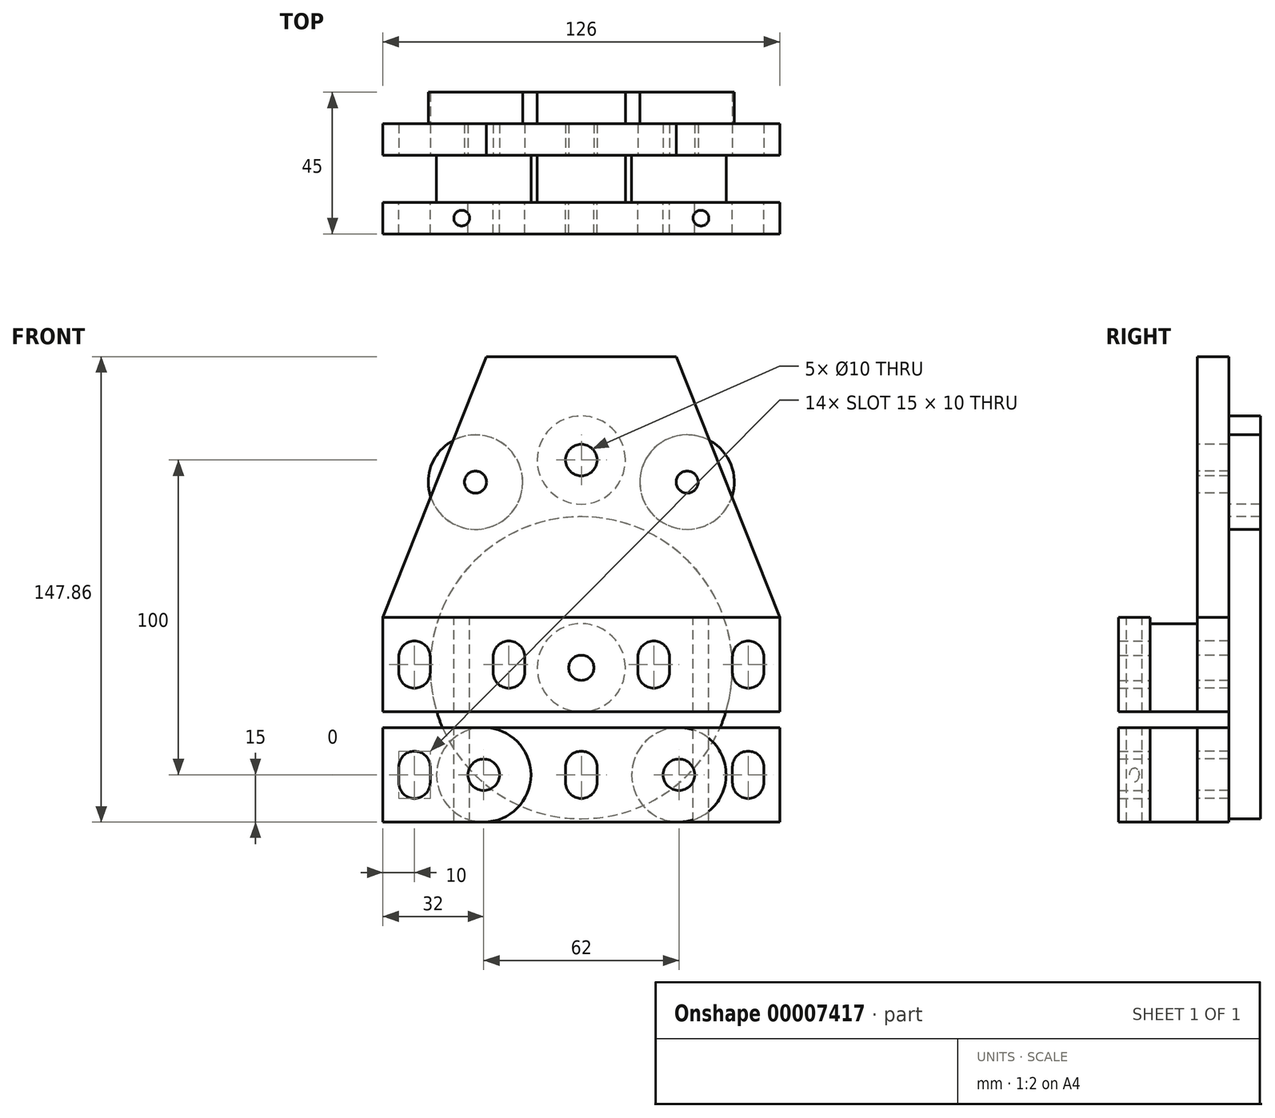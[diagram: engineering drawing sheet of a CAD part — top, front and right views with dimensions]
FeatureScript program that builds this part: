
annotation { "Feature Type Name" : "Feature", "Feature Type Description" : "" }
export const myFeature = defineFeature(function(context is Context, id is Id, definition is map)
    precondition{}
    {
        {
            var Q0;
            Q0=qCreatedBy(makeId("Front.planeOp"),FACE);
            var sketch = newSketch(context, id + "F0", { "sketchPlane" : qUnion([Q0])});
            skCircle(sketch, "E0", {"center": v(0, 0) * mm, "radius": 14 * mm});
            skCircle(sketch, "E1", {"center": v(0, 0) * mm, "radius": 48 * mm});
            skLineSegment(sketch, "E2", {"start": v(-81.34, -49) * mm, "end": v(130.56, -49) * mm, "construction": true});
            skCircle(sketch, "E3", {"center": v(-31, -34) * mm, "radius": 15 * mm});
            skLineSegment(sketch, "E4", {"start": v(0, 0) * mm, "end": v(0, -49) * mm, "construction": true});
            skLineSegment(sketch, "E5", {"start": v(-81.34, -52.2) * mm, "end": v(130.56, -52.2) * mm, "construction": true});
            skLineSegment(sketch, "E6", {"start": v(130.56, -51.2) * mm, "end": v(-81.34, -51.2) * mm, "construction": true});
            skCircle(sketch, "E7.MirrorC", {"center": v(31, -34) * mm, "radius": 15 * mm});
            skCircle(sketch, "E8", {"center": v(-63, -34) * mm, "radius": 15 * mm, "construction": true});
            skCircle(sketch, "E9.MirrorC", {"center": v(63, -34) * mm, "radius": 15 * mm, "construction": true});
            skLineSegment(sketch, "E10", {"start": v(71.6, 114.85) * mm, "end": v(71.6, 34.85) * mm});
            skLineSegment(sketch, "E11", {"start": v(71.6, 34.85) * mm, "end": v(91.6, 34.85) * mm});
            skLineSegment(sketch, "E12", {"start": v(91.6, 34.85) * mm, "end": v(91.6, 64.85) * mm});
            skLineSegment(sketch, "E13", {"start": v(91.6, 64.85) * mm, "end": v(141.6, 64.85) * mm});
            skLineSegment(sketch, "E14", {"start": v(141.6, 64.85) * mm, "end": v(141.6, 34.85) * mm});
            skLineSegment(sketch, "E15", {"start": v(141.6, 34.85) * mm, "end": v(161.6, 34.85) * mm});
            skLineSegment(sketch, "E16", {"start": v(161.6, 34.85) * mm, "end": v(161.6, 114.85) * mm});
            skLineSegment(sketch, "E17", {"start": v(161.6, 114.85) * mm, "end": v(71.6, 114.85) * mm});
            skLineSegment(sketch, "E18", {"start": v(-14, 0) * mm, "end": v(-14, -49) * mm, "construction": true});
            skLineSegment(sketch, "E19", {"start": v(-16, -34) * mm, "end": v(-14, -34) * mm, "construction": true});
            skLineSegment(sketch, "E20", {"start": v(-31, -19) * mm, "end": v(0, -19) * mm, "construction": true});
            skPoint(sketch, "E21", {"position": v(0, -14) * mm});
            skSolve(sketch);
        }
        {
            var Q0;
            Q0=qCreatedBy(makeId("Front.planeOp"),FACE);
            var sketch = newSketch(context, id + "F1", { "sketchPlane" : qUnion([Q0])});
            skCircle(sketch, "E22.0", {"center": v(0, 0) * mm, "radius": 14 * mm, "construction": true});
            skLineSegment(sketch, "E23", {"start": v(-63, 16) * mm, "end": v(-63, -14) * mm});
            skLineSegment(sketch, "E24", {"start": v(-63, -14) * mm, "end": v(63, -14) * mm});
            skLineSegment(sketch, "E25", {"start": v(63, -14) * mm, "end": v(63, 16) * mm});
            skLineSegment(sketch, "E26", {"start": v(63, 16) * mm, "end": v(-63, 16) * mm});
            skCircle(sketch, "E27", {"center": v(0, 0) * mm, "radius": 4 * mm});
            skLineSegment(sketch, "E28.bottom", {"start": v(-63, -19) * mm, "end": v(63, -19) * mm});
            skLineSegment(sketch, "E28.top", {"start": v(-63, -49) * mm, "end": v(63, -49) * mm});
            skLineSegment(sketch, "E28.left", {"start": v(-63, -19) * mm, "end": v(-63, -49) * mm});
            skLineSegment(sketch, "E28.right", {"start": v(63, -19) * mm, "end": v(63, -49) * mm});
            skLineSegment(sketch, "E29", {"start": v(0, 0) * mm, "end": v(0, -19) * mm, "construction": true});
            skLineSegment(sketch, "E30", {"start": v(-48, -34) * mm, "end": v(-46, -34) * mm, "construction": true});
            skLineSegment(sketch, "E31", {"start": v(-46, -34) * mm, "end": v(-31, -34) * mm, "construction": true});
            skLineSegment(sketch, "E32", {"start": v(-53, -36.5) * mm, "end": v(-53, -31.5) * mm, "construction": true});
            skArc(sketch, "E33.0.startCap", {"start": v(-48, -36.5) * mm, "mid": v(-53, -41.5) * mm, "end": v(-58, -36.5) * mm});
            skArc(sketch, "E33.0.endCap", {"start": v(-58, -31.5) * mm, "mid": v(-53, -26.5) * mm, "end": v(-48, -31.5) * mm});
            skLineSegment(sketch, "E33.0.left", {"start": v(-58, -36.5) * mm, "end": v(-58, -31.5) * mm});
            skLineSegment(sketch, "E33.0.right", {"start": v(-48, -36.5) * mm, "end": v(-48, -31.5) * mm});
            skLineSegment(sketch, "E34", {"start": v(-58, -34) * mm, "end": v(-63, -34) * mm, "construction": true});
            skLineSegment(sketch, "E35", {"start": v(0, -31.5) * mm, "end": v(0, -36.5) * mm, "construction": true});
            skArc(sketch, "E36.0.startCap", {"start": v(-5, -31.5) * mm, "mid": v(0, -26.5) * mm, "end": v(5, -31.5) * mm});
            skArc(sketch, "E36.0.endCap", {"start": v(5, -36.5) * mm, "mid": v(0, -41.5) * mm, "end": v(-5, -36.5) * mm});
            skLineSegment(sketch, "E36.0.left", {"start": v(5, -31.5) * mm, "end": v(5, -36.5) * mm});
            skLineSegment(sketch, "E36.0.right", {"start": v(-5, -31.5) * mm, "end": v(-5, -36.5) * mm});
            skLineSegment(sketch, "E37", {"start": v(-31, -34) * mm, "end": v(0, -34) * mm, "construction": true});
            skArc(sketch, "E38.MirrorCS", {"start": v(58, -31.5) * mm, "mid": v(53, -26.5) * mm, "end": v(48, -31.5) * mm});
            skLineSegment(sketch, "E39.MirrorCS", {"start": v(58, -36.5) * mm, "end": v(58, -31.5) * mm});
            skArc(sketch, "E40.MirrorCS", {"start": v(48, -36.5) * mm, "mid": v(53, -41.5) * mm, "end": v(58, -36.5) * mm});
            skLineSegment(sketch, "E41.MirrorCS", {"start": v(48, -36.5) * mm, "end": v(48, -31.5) * mm});
            skCircle(sketch, "E42", {"center": v(-31, -34) * mm, "radius": 5 * mm});
            skCircle(sketch, "E43", {"center": v(31, -34) * mm, "radius": 5 * mm});
            skLineSegment(sketch, "E44", {"start": v(-53, 3.5) * mm, "end": v(-53, -1.5) * mm, "construction": true});
            skArc(sketch, "E45.0.startCap", {"start": v(-58, 3.5) * mm, "mid": v(-53, 8.5) * mm, "end": v(-48, 3.5) * mm});
            skArc(sketch, "E45.0.endCap", {"start": v(-48, -1.5) * mm, "mid": v(-53, -6.5) * mm, "end": v(-58, -1.5) * mm});
            skLineSegment(sketch, "E45.0.left", {"start": v(-48, 3.5) * mm, "end": v(-48, -1.5) * mm});
            skLineSegment(sketch, "E45.0.right", {"start": v(-58, 3.5) * mm, "end": v(-58, -1.5) * mm});
            skArc(sketch, "E46.0.startCap", {"start": v(-58, 3.5) * mm, "mid": v(-53, 8.5) * mm, "end": v(-48, 3.5) * mm, "construction": true});
            skArc(sketch, "E46.0.endCap", {"start": v(-48, -1.5) * mm, "mid": v(-53, -6.5) * mm, "end": v(-58, -1.5) * mm, "construction": true});
            skLineSegment(sketch, "E46.0.left", {"start": v(-48, 3.5) * mm, "end": v(-48, -1.5) * mm, "construction": true});
            skLineSegment(sketch, "E46.0.right", {"start": v(-58, 3.5) * mm, "end": v(-58, -1.5) * mm, "construction": true});
            skLineSegment(sketch, "E47", {"start": v(-58, 1) * mm, "end": v(-63, 1) * mm, "construction": true});
            skLineSegment(sketch, "E48", {"start": v(-38, -14) * mm, "end": v(-38, 16) * mm, "construction": true});
            skArc(sketch, "E49.MirrorCS", {"start": v(-18, 3.5) * mm, "mid": v(-23, 8.5) * mm, "end": v(-28, 3.5) * mm});
            skLineSegment(sketch, "E50.MirrorCS", {"start": v(-18, 3.5) * mm, "end": v(-18, -1.5) * mm});
            skArc(sketch, "E51.MirrorCS", {"start": v(-28, -1.5) * mm, "mid": v(-23, -6.5) * mm, "end": v(-18, -1.5) * mm});
            skLineSegment(sketch, "E52.MirrorCS", {"start": v(-28, 3.5) * mm, "end": v(-28, -1.5) * mm});
            skLineSegment(sketch, "E53", {"start": v(-48, 1) * mm, "end": v(-38, 1) * mm, "construction": true});
            skLineSegment(sketch, "E54.MirrorCS", {"start": v(28, 3.5) * mm, "end": v(28, -1.5) * mm});
            skArc(sketch, "E55.MirrorCS", {"start": v(18, 3.5) * mm, "mid": v(23, 8.5) * mm, "end": v(28, 3.5) * mm});
            skLineSegment(sketch, "E56.MirrorCS", {"start": v(18, 3.5) * mm, "end": v(18, -1.5) * mm});
            skArc(sketch, "E57.MirrorCS", {"start": v(28, -1.5) * mm, "mid": v(23, -6.5) * mm, "end": v(18, -1.5) * mm});
            skArc(sketch, "E58.MirrorCS", {"start": v(48, -1.5) * mm, "mid": v(53, -6.5) * mm, "end": v(58, -1.5) * mm});
            skArc(sketch, "E59.MirrorCS", {"start": v(58, 3.5) * mm, "mid": v(53, 8.5) * mm, "end": v(48, 3.5) * mm});
            skLineSegment(sketch, "E60.MirrorCS", {"start": v(48, 3.5) * mm, "end": v(48, -1.5) * mm});
            skLineSegment(sketch, "E61.MirrorCS", {"start": v(58, 3.5) * mm, "end": v(58, -1.5) * mm});
            skLineSegment(sketch, "E62.MirrorCS", {"start": v(48, 3.5) * mm, "end": v(48, -1.5) * mm, "construction": true});
            skArc(sketch, "E63.MirrorCS", {"start": v(48, -1.5) * mm, "mid": v(53, -6.5) * mm, "end": v(58, -1.5) * mm, "construction": true});
            skArc(sketch, "E64.MirrorCS", {"start": v(58, 3.5) * mm, "mid": v(53, 8.5) * mm, "end": v(48, 3.5) * mm, "construction": true});
            skLineSegment(sketch, "E65.MirrorCS", {"start": v(58, 3.5) * mm, "end": v(58, -1.5) * mm, "construction": true});
            skLineSegment(sketch, "E66.bottom", {"start": v(-30, 96) * mm, "end": v(30, 96) * mm, "construction": true});
            skLineSegment(sketch, "E66.top", {"start": v(-30, 36) * mm, "end": v(30, 36) * mm, "construction": true});
            skLineSegment(sketch, "E66.left", {"start": v(-30, 96) * mm, "end": v(-30, 36) * mm, "construction": true});
            skLineSegment(sketch, "E66.right", {"start": v(30, 96) * mm, "end": v(30, 36) * mm, "construction": true});
            skLineSegment(sketch, "E67", {"start": v(0, 16) * mm, "end": v(0, 36) * mm, "construction": true});
            skCircle(sketch, "E68", {"center": v(0, 66) * mm, "radius": 14 * mm, "construction": true});
            skPoint(sketch, "E68.centerSnap0", {"position": v(30, 66) * mm});
            skPoint(sketch, "E68.centerSnap1", {"position": v(0, 96) * mm});
            skSolve(sketch);
        }
        {
            var Q0;
            Q0 = qSketchRegion(id + "F1", true);
            extrude(context, id + "F2", {"entities" : qUnion([Q0]), "depth" : 10 * mm});
        }
        {
            var Q0;
            Q0=makeQuery(id+"F2.opExtrude","SWEPT_FACE",FACE,{"disambiguationData":[OSD([sQuery(id+"F1.wireOp",EDGE,"E26")])]});
            var sketch = newSketch(context, id + "F3", { "sketchPlane" : qUnion([Q0])});
            skPoint(sketch, "E69.0", {"position": v(-28, -10) * mm});
            skPoint(sketch, "E69.1", {"position": v(-48, -10) * mm});
            skCircle(sketch, "E70", {"center": v(-38, -5) * mm, "radius": 2.5 * mm});
            skLineSegment(sketch, "E71", {"start": v(-38, -5) * mm, "end": v(-28, -5) * mm, "construction": true});
            skLineSegment(sketch, "E72", {"start": v(-38, -5) * mm, "end": v(-48, -5) * mm, "construction": true});
            skLineSegment(sketch, "E73", {"start": v(-28, -5) * mm, "end": v(-28, 0) * mm, "construction": true});
            skLineSegment(sketch, "E74", {"start": v(-28, -5) * mm, "end": v(-28, -10) * mm, "construction": true});
            skLineSegment(sketch, "E75", {"start": v(0, 0) * mm, "end": v(0, -10) * mm, "construction": true});
            skCircle(sketch, "E76.MirrorC", {"center": v(38, -5) * mm, "radius": 2.5 * mm});
            skSolve(sketch);
        }
        {
            var Q0;
            Q0 = qSketchRegion(id + "F3", true);
            extrude(context, id + "F4", {"entities" : qUnion([Q0]), "operationType" : NewBodyOperationType.REMOVE, "endBound" : BoundingType.THROUGH_ALL, "oppositeDirection" : true, "depth" : 25 * mm});
        }
        {
            var Q0;
            Q0=makeQuery(id+"F2.opExtrude","CAP_FACE",FACE,{"disambiguationData":[OSD([sQuery(id+"F1.wireOp",EDGE,"E23"),sQuery(id+"F1.wireOp",EDGE,"E24"),sQuery(id+"F1.wireOp",EDGE,"E25"),sQuery(id+"F1.wireOp",EDGE,"E26"),sQuery(id+"F1.wireOp",EDGE,"E27"),sQuery(id+"F1.wireOp",EDGE,"E45.0.startCap"),sQuery(id+"F1.wireOp",EDGE,"E45.0.endCap"),sQuery(id+"F1.wireOp",EDGE,"E45.0.left"),sQuery(id+"F1.wireOp",EDGE,"E45.0.right"),sQuery(id+"F1.wireOp",EDGE,"E49.MirrorCS"),sQuery(id+"F1.wireOp",EDGE,"E50.MirrorCS"),sQuery(id+"F1.wireOp",EDGE,"E51.MirrorCS"),sQuery(id+"F1.wireOp",EDGE,"E52.MirrorCS"),sQuery(id+"F1.wireOp",EDGE,"E54.MirrorCS"),sQuery(id+"F1.wireOp",EDGE,"E55.MirrorCS"),sQuery(id+"F1.wireOp",EDGE,"E56.MirrorCS"),sQuery(id+"F1.wireOp",EDGE,"E57.MirrorCS"),sQuery(id+"F1.wireOp",EDGE,"E58.MirrorCS"),sQuery(id+"F1.wireOp",EDGE,"E59.MirrorCS"),sQuery(id+"F1.wireOp",EDGE,"E60.MirrorCS"),sQuery(id+"F1.wireOp",EDGE,"E61.MirrorCS")])],"isStart":true});
            cPlane(context, id + "F5", {"entities" : qUnion([Q0]), "cplaneType" : CPlaneType.OFFSET, "offset" : 15 * mm, "width" : 150 * mm, "height" : 150 * mm});
        }
        {
            var Q0;
            Q0=qCreatedBy(id+"F5.planeOp",FACE);
            var sketch = newSketch(context, id + "F6", { "sketchPlane" : qUnion([Q0])});
            skLineSegment(sketch, "E77.0.0", {"start": v(63, -19) * mm, "end": v(63, -49) * mm});
            skLineSegment(sketch, "E77.0.1", {"start": v(63, -49) * mm, "end": v(-63, -49) * mm});
            skLineSegment(sketch, "E77.0.2", {"start": v(-63, -49) * mm, "end": v(-63, -19) * mm});
            skLineSegment(sketch, "E77.0.3", {"start": v(-63, -19) * mm, "end": v(63, -19) * mm});
            skLineSegment(sketch, "E78.0.0", {"start": v(-63, -14) * mm, "end": v(-63, 16) * mm});
            skLineSegment(sketch, "E78.0.1", {"start": v(-63, 16) * mm, "end": v(63, 16) * mm, "construction": true});
            skLineSegment(sketch, "E78.0.2", {"start": v(63, 16) * mm, "end": v(63, -14) * mm});
            skLineSegment(sketch, "E78.0.3", {"start": v(63, -14) * mm, "end": v(-63, -14) * mm});
            skArc(sketch, "E79.0", {"start": v(-48, -36.5) * mm, "mid": v(-53, -41.5) * mm, "end": v(-58, -36.5) * mm});
            skLineSegment(sketch, "E79.1", {"start": v(-58, -36.5) * mm, "end": v(-58, -31.5) * mm});
            skArc(sketch, "E79.2", {"start": v(-58, -31.5) * mm, "mid": v(-53, -26.5) * mm, "end": v(-48, -31.5) * mm});
            skLineSegment(sketch, "E79.3", {"start": v(-48, -36.5) * mm, "end": v(-48, -31.5) * mm});
            skCircle(sketch, "E79.4", {"center": v(-31, -34) * mm, "radius": 5 * mm});
            skArc(sketch, "E79.5", {"start": v(5, -31.5) * mm, "mid": v(0, -26.5) * mm, "end": v(-5, -31.5) * mm});
            skLineSegment(sketch, "E79.6", {"start": v(-5, -31.5) * mm, "end": v(-5, -36.5) * mm});
            skArc(sketch, "E79.7", {"start": v(-5, -36.5) * mm, "mid": v(0, -41.5) * mm, "end": v(5, -36.5) * mm});
            skLineSegment(sketch, "E79.8", {"start": v(5, -31.5) * mm, "end": v(5, -36.5) * mm});
            skCircle(sketch, "E79.9", {"center": v(31, -34) * mm, "radius": 5 * mm});
            skArc(sketch, "E79.10", {"start": v(58, -31.5) * mm, "mid": v(53, -26.5) * mm, "end": v(48, -31.5) * mm});
            skLineSegment(sketch, "E79.11", {"start": v(48, -36.5) * mm, "end": v(48, -31.5) * mm});
            skArc(sketch, "E79.12", {"start": v(48, -36.5) * mm, "mid": v(53, -41.5) * mm, "end": v(58, -36.5) * mm});
            skLineSegment(sketch, "E79.13", {"start": v(58, -36.5) * mm, "end": v(58, -31.5) * mm});
            skArc(sketch, "E80.0", {"start": v(-58, 3.5) * mm, "mid": v(-53, 8.5) * mm, "end": v(-48, 3.5) * mm});
            skArc(sketch, "E80.1", {"start": v(-48, -1.5) * mm, "mid": v(-53, -6.5) * mm, "end": v(-58, -1.5) * mm});
            skLineSegment(sketch, "E80.2", {"start": v(-48, 3.5) * mm, "end": v(-48, -1.5) * mm});
            skLineSegment(sketch, "E80.3", {"start": v(-58, 3.5) * mm, "end": v(-58, -1.5) * mm});
            skLineSegment(sketch, "E80.4", {"start": v(-28, 3.5) * mm, "end": v(-28, -1.5) * mm});
            skArc(sketch, "E80.5", {"start": v(-18, 3.5) * mm, "mid": v(-23, 8.5) * mm, "end": v(-28, 3.5) * mm});
            skLineSegment(sketch, "E80.6", {"start": v(-18, 3.5) * mm, "end": v(-18, -1.5) * mm});
            skArc(sketch, "E80.7", {"start": v(-28, -1.5) * mm, "mid": v(-23, -6.5) * mm, "end": v(-18, -1.5) * mm});
            skCircle(sketch, "E80.8", {"center": v(0, 0) * mm, "radius": 4 * mm});
            skLineSegment(sketch, "E81.0", {"start": v(18, 3.5) * mm, "end": v(18, -1.5) * mm});
            skArc(sketch, "E81.1", {"start": v(18, 3.5) * mm, "mid": v(23, 8.5) * mm, "end": v(28, 3.5) * mm});
            skArc(sketch, "E81.2", {"start": v(28, -1.5) * mm, "mid": v(23, -6.5) * mm, "end": v(18, -1.5) * mm});
            skLineSegment(sketch, "E81.3", {"start": v(28, 3.5) * mm, "end": v(28, -1.5) * mm});
            skArc(sketch, "E81.4", {"start": v(58, 3.5) * mm, "mid": v(53, 8.5) * mm, "end": v(48, 3.5) * mm});
            skLineSegment(sketch, "E81.5", {"start": v(48, 3.5) * mm, "end": v(48, -1.5) * mm});
            skArc(sketch, "E81.6", {"start": v(48, -1.5) * mm, "mid": v(53, -6.5) * mm, "end": v(58, -1.5) * mm});
            skLineSegment(sketch, "E81.7", {"start": v(58, 3.5) * mm, "end": v(58, -1.5) * mm});
            skCircle(sketch, "E82.0", {"center": v(0, 66) * mm, "radius": 14 * mm, "construction": true});
            skLineSegment(sketch, "E83", {"start": v(-63, 16) * mm, "end": v(-30.2, 98.86) * mm});
            skLineSegment(sketch, "E84", {"start": v(63, 16) * mm, "end": v(30.2, 98.86) * mm});
            skLineSegment(sketch, "E85.bottom", {"start": v(28.5, 94.5) * mm, "end": v(-28.5, 94.5) * mm, "construction": true});
            skLineSegment(sketch, "E85.top", {"start": v(28.5, 37.5) * mm, "end": v(-28.5, 37.5) * mm, "construction": true});
            skLineSegment(sketch, "E85.left", {"start": v(28.5, 94.5) * mm, "end": v(28.5, 37.5) * mm, "construction": true});
            skLineSegment(sketch, "E85.right", {"start": v(-28.5, 94.5) * mm, "end": v(-28.5, 37.5) * mm, "construction": true});
            skLineSegment(sketch, "E86", {"start": v(30.2, 98.86) * mm, "end": v(-30.2, 98.86) * mm});
            skLineSegment(sketch, "E87", {"start": v(0, 98.86) * mm, "end": v(0, 66) * mm, "construction": true});
            skCircle(sketch, "E88", {"center": v(0, 66) * mm, "radius": 5 * mm});
            skCircle(sketch, "E89.0", {"center": v(0, 0) * mm, "radius": 48 * mm, "construction": true});
            skCircle(sketch, "E90", {"center": v(-33.6, 58.99) * mm, "radius": 3.5 * mm});
            skCircle(sketch, "E91", {"center": v(-33.6, 58.99) * mm, "radius": 15 * mm, "construction": true});
            skCircle(sketch, "E92.MirrorC", {"center": v(33.6, 58.99) * mm, "radius": 15 * mm, "construction": true});
            skCircle(sketch, "E93.MirrorC", {"center": v(33.6, 58.99) * mm, "radius": 3.5 * mm});
            skSolve(sketch);
        }
        {
            var Q0;
            Q0 = qSketchRegion(id + "F6", true);
            extrude(context, id + "F7", {"entities" : qUnion([Q0]), "depth" : 10 * mm});
        }
        {
            var Q0;
            {var subQ0=sQuery(id+"F0.wireOp",EDGE,"E7.MirrorC");var subQ1=sQuery(id+"F0.wireOp",EDGE,"E1");var subQ2=makeQuery(id+"F0.imprint","INTERSECT",VERTEX,{"disambiguationData":[OD(0.0)],"derivedFrom":[subQ1,subQ0]});Q0=makeQuery(id+"F0.imprint","IMPRINT",FACE,{"disambiguationData":[TD([[makeQuery(id+"F0.imprint","IMPRINT",EDGE,{"disambiguationData":[TD([[subQ2,-1.0]])],"derivedFrom":subQ1}),-1.0]])]});}
            var Q1;
            {var subQ0=sQuery(id+"F0.wireOp",EDGE,"E7.MirrorC");var subQ1=sQuery(id+"F0.wireOp",EDGE,"E1");var subQ2=makeQuery(id+"F0.imprint","INTERSECT",VERTEX,{"disambiguationData":[OD(0.0)],"derivedFrom":[subQ1,subQ0]});Q1=makeQuery(id+"F0.imprint","IMPRINT",FACE,{"disambiguationData":[TD([[makeQuery(id+"F0.imprint","IMPRINT",EDGE,{"disambiguationData":[TD([[subQ2,-1.0]])],"derivedFrom":subQ1}),1.0]])]});}
            var Q2;
            Q2=makeQuery(id+"F0.imprint","IMPRINT",FACE,{"disambiguationData":[TD([[makeQuery(id+"F0.imprint","IMPRINT",EDGE,{"derivedFrom":sQuery(id+"F0.wireOp",EDGE,"E0")}),1.0]])]});
            var Q3;
            {var subQ0=sQuery(id+"F0.wireOp",EDGE,"E3");var subQ1=sQuery(id+"F0.wireOp",EDGE,"E1");var subQ2=makeQuery(id+"F0.imprint","INTERSECT",VERTEX,{"disambiguationData":[OD(0.0)],"derivedFrom":[subQ1,subQ0]});Q3=makeQuery(id+"F0.imprint","IMPRINT",FACE,{"disambiguationData":[TD([[makeQuery(id+"F0.imprint","IMPRINT",EDGE,{"disambiguationData":[TD([[subQ2,1.0]])],"derivedFrom":subQ1}),1.0]])]});}
            var Q4;
            {var subQ0=sQuery(id+"F0.wireOp",EDGE,"E3");var subQ1=sQuery(id+"F0.wireOp",EDGE,"E1");var subQ2=makeQuery(id+"F0.imprint","INTERSECT",VERTEX,{"disambiguationData":[OD(0.0)],"derivedFrom":[subQ1,subQ0]});Q4=makeQuery(id+"F0.imprint","IMPRINT",FACE,{"disambiguationData":[TD([[makeQuery(id+"F0.imprint","IMPRINT",EDGE,{"disambiguationData":[TD([[subQ2,1.0]])],"derivedFrom":subQ1}),-1.0]])]});}
            extrude(context, id + "F8", {"entities" : qUnion([Q0, Q1, Q2, Q3, Q4]), "oppositeDirection" : true, "depth" : 15 * mm});
        }
        {
            var Q0;
            Q0=makeQuery(id+"F7.opExtrude","CAP_FACE",FACE,{"disambiguationData":[OSD([sQuery(id+"F6.wireOp",EDGE,"E78.0.0"),sQuery(id+"F6.wireOp",EDGE,"E78.0.2"),sQuery(id+"F6.wireOp",EDGE,"E78.0.3"),sQuery(id+"F6.wireOp",EDGE,"E80.0"),sQuery(id+"F6.wireOp",EDGE,"E80.1"),sQuery(id+"F6.wireOp",EDGE,"E80.2"),sQuery(id+"F6.wireOp",EDGE,"E80.3"),sQuery(id+"F6.wireOp",EDGE,"E80.4"),sQuery(id+"F6.wireOp",EDGE,"E80.5"),sQuery(id+"F6.wireOp",EDGE,"E80.6"),sQuery(id+"F6.wireOp",EDGE,"E80.7"),sQuery(id+"F6.wireOp",EDGE,"E80.8"),sQuery(id+"F6.wireOp",EDGE,"E81.0"),sQuery(id+"F6.wireOp",EDGE,"E81.1"),sQuery(id+"F6.wireOp",EDGE,"E81.2"),sQuery(id+"F6.wireOp",EDGE,"E81.3"),sQuery(id+"F6.wireOp",EDGE,"E81.4"),sQuery(id+"F6.wireOp",EDGE,"E81.5"),sQuery(id+"F6.wireOp",EDGE,"E81.6"),sQuery(id+"F6.wireOp",EDGE,"E81.7"),sQuery(id+"F6.wireOp",EDGE,"E83"),sQuery(id+"F6.wireOp",EDGE,"E84"),sQuery(id+"F6.wireOp",EDGE,"E86"),sQuery(id+"F6.wireOp",EDGE,"E88"),sQuery(id+"F6.wireOp",EDGE,"E90"),sQuery(id+"F6.wireOp",EDGE,"E93.MirrorC")])],"isStart":false});
            var sketch = newSketch(context, id + "F9", { "sketchPlane" : qUnion([Q0])});
            skCircle(sketch, "E94.0", {"center": v(0, 0) * mm, "radius": 48 * mm});
            skCircle(sketch, "E94.1", {"center": v(-33.6, 58.99) * mm, "radius": 15 * mm});
            skCircle(sketch, "E94.2", {"center": v(33.6, 58.99) * mm, "radius": 15 * mm});
            skCircle(sketch, "E95.0", {"center": v(0, 66) * mm, "radius": 14 * mm});
            skSolve(sketch);
        }
        {
            var Q0;
            Q0 = qSketchRegion(id + "F9", true);
            extrude(context, id + "F10", {"entities" : qUnion([Q0]), "depth" : 10 * mm});
        }
    });
